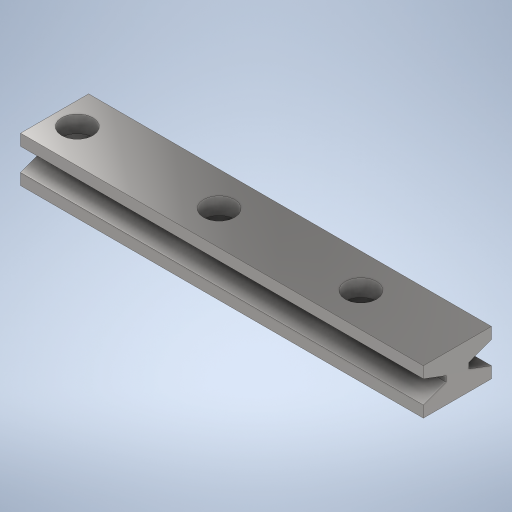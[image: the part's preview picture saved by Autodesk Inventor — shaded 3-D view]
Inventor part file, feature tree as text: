
AUTODESK INVENTOR PART (.ipt)
format: ipt  version: 2024.2 (Build 282272000, 272)  size: 306,176 bytes
history: native  units: in
note: dims shown in document units (in); Inventor stores cm internally (conversion verified against a paired STEP export)
features: sketch x2, extrude x1, hole x1
ambient origin geometry x8: Origin, YZ Plane, XZ Plane, XY Plane, X Axis, Y Axis, Z Axis, Center Point
bodies: Solid1 (feature_tree)
feature tree (4):
  extrude  "Extrusion1"  Depth=0.4724in
  hole  "Hole1"  [1 undecoded]
  sketch  "Sketch1"  dims[d3=0.315in d4=0.4724in]
  sketch  "Sketch2"  dims[d5=0.1575in d6=0.0787in d7=0.0787in d15=2.7953in d16=0.0in d17=0.0787in d18=0.0787in d19=0.0394in d20=0.0394in d21=0.1575in d22=0.1575in d23=0.9843in d24=0.0968in d25=0.2362in d26=0.2165in d27=0.1181in d28=90.0deg d29=0.315in d30=0.8108in d31=0.9843in]
note: 1 required parameter value undecoded (feature->parameter linkage not recoverable at this tier; creation-order binding heuristic only, values carry confidence <= 0.55)
